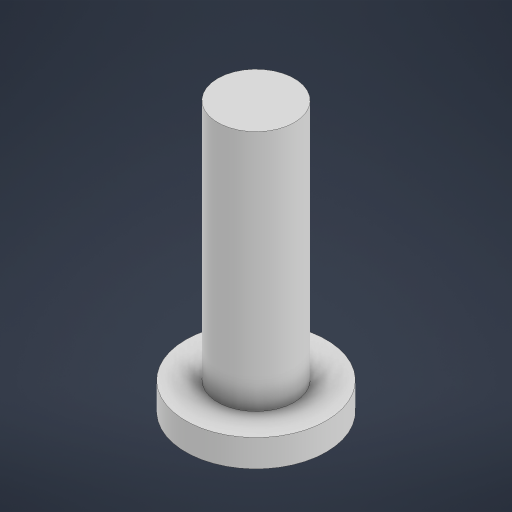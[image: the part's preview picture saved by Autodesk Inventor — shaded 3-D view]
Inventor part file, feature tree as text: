
AUTODESK INVENTOR PART (.ipt)
format: ipt  version: 2023 (Build 270158030, 158C)  size: 176,640 bytes
history: native  units: in
note: dims shown in document units (in); Inventor stores cm internally (conversion verified against a paired STEP export)
features: extrude x2, sketch x2
ambient origin geometry x8: Origin, YZ Plane, XZ Plane, XY Plane, X Axis, Y Axis, Z Axis, Center Point
bodies: Body1 (feature_tree)
feature tree (4):
  extrude  "Extrusion4"  Depth=0.1102in TaperAngle=0.0deg
  extrude  "Extrusion5"  Depth=0.9843in TaperAngle=0.0deg
  sketch  "Sketch5"  dims[d9=0.5709in d10=0.1102in d11=0.0in]
  sketch  "Sketch6"  dims[d12=0.311in d13=0.9843in d14=0.0in d15=0.0197in d16=0.0344in d17=0.0197in d18=0.0344in]
